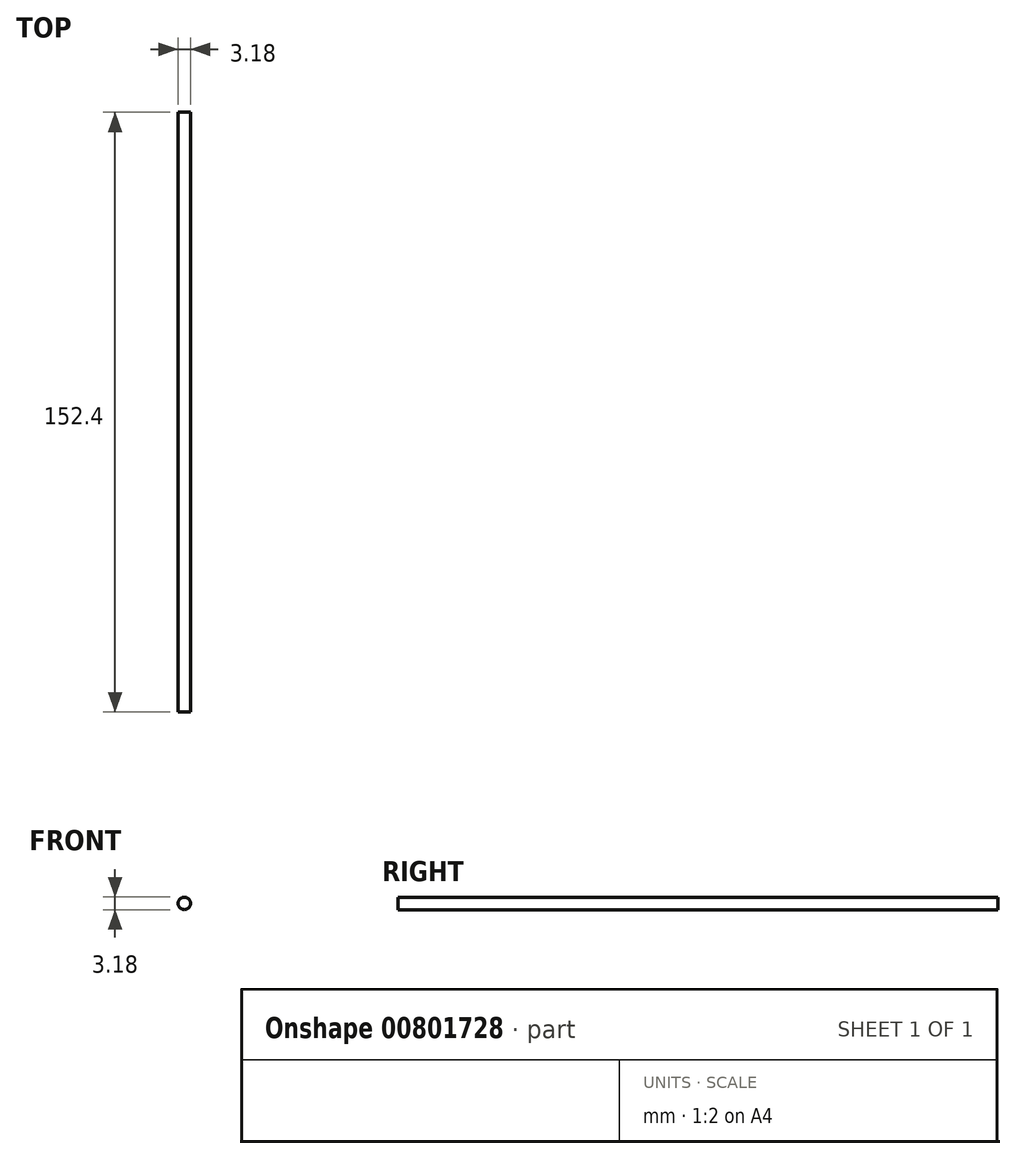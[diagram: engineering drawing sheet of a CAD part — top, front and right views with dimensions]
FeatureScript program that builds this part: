
annotation { "Feature Type Name" : "Feature", "Feature Type Description" : "" }
export const myFeature = defineFeature(function(context is Context, id is Id, definition is map)
    precondition{}
    {
        {
            var Q0;
            Q0=qCreatedBy(makeId("Front.planeOp"),FACE);
            var sketch = newSketch(context, id + "F0", { "sketchPlane" : qUnion([Q0])});
            skCircle(sketch, "E0", {"center": v(0, 0) * mm, "radius": 1.59 * mm});
            skSolve(sketch);
        }
        {
            var Q0;
            Q0 = qSketchRegion(id + "F0", true);
            extrude(context, id + "F1", {"entities" : qUnion([Q0]), "depth" : 152.4 * mm, "offsetDistance" : 25.4 * mm, "symmetric" : true});
        }
    });
